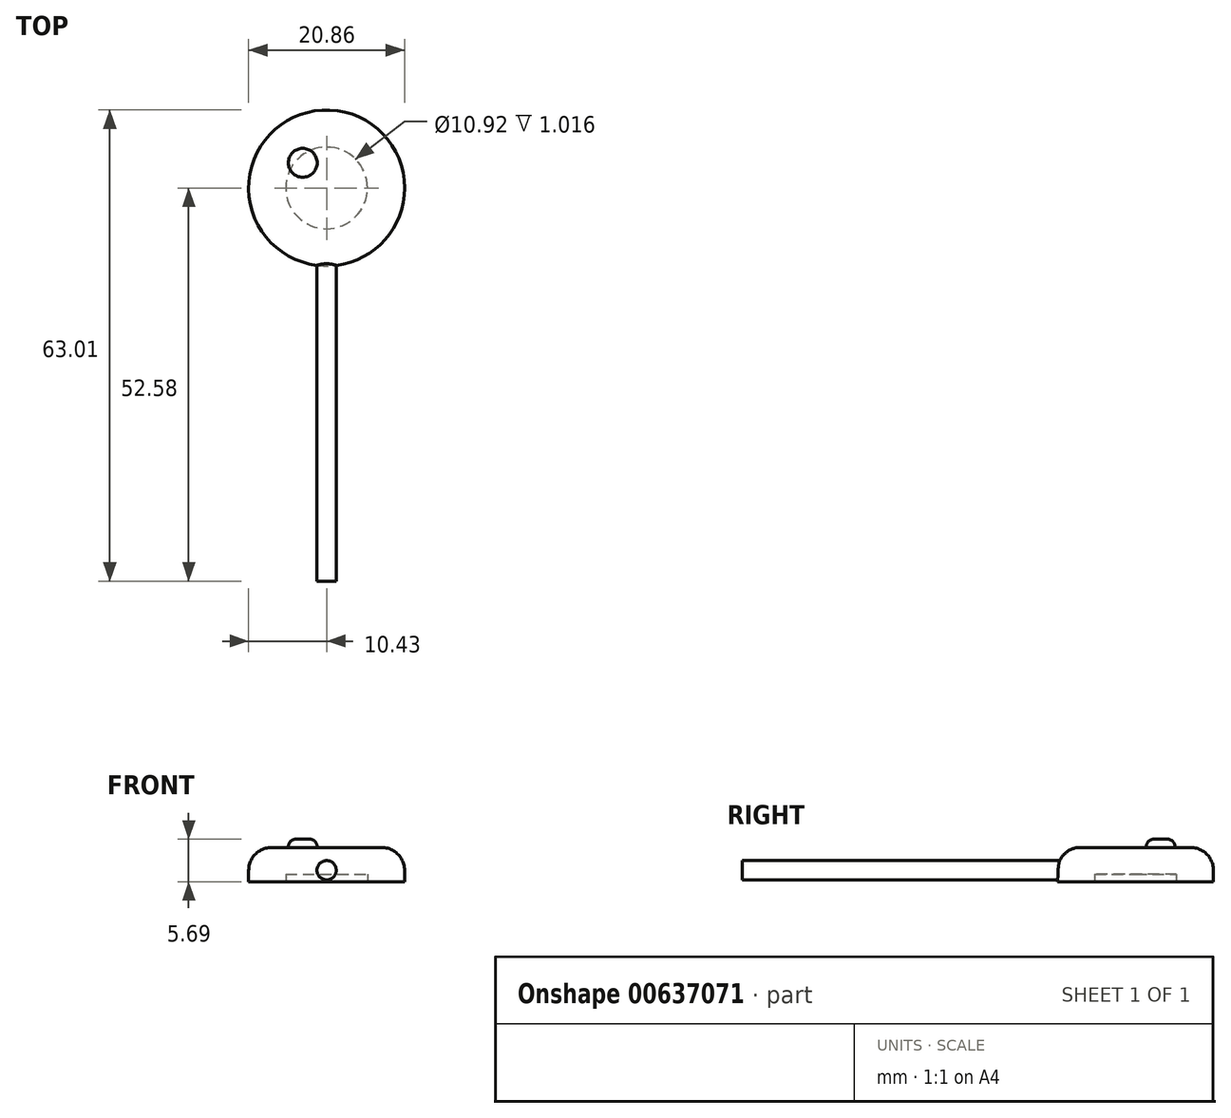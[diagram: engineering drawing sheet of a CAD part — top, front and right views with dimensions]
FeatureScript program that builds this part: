
annotation { "Feature Type Name" : "Feature", "Feature Type Description" : "" }
export const myFeature = defineFeature(function(context is Context, id is Id, definition is map)
    precondition{}
    {
        {
            var Q0;
            Q0=qCreatedBy(makeId("Top.planeOp"),FACE);
            var sketch = newSketch(context, id + "F0", { "sketchPlane" : qUnion([Q0])});
            skCircle(sketch, "E0", {"center": v(0, 0) * mm, "radius": 10.43 * mm});
            skSolve(sketch);
        }
        {
            var Q0;
            Q0=makeQuery(id+"F0.imprint","IMPRINT",FACE,{"disambiguationData":[TD([[makeQuery(id+"F0.imprint","IMPRINT",EDGE,{"derivedFrom":sQuery(id+"F0.wireOp",EDGE,"E0")}),1.0]])]});
            extrude(context, id + "F1", {"entities" : qUnion([Q0]), "depth" : 4.57 * mm, "offsetDistance" : 25.4 * mm});
        }
        {
            var Q0;
            Q0=makeQuery(id+"F1.opExtrude","CAP_EDGE",EDGE,{"disambiguationData":[OSD([sQuery(id+"F0.wireOp",EDGE,"E0")])],"isStart":false});
            fillet(context, id + "F2", {"entities" : qUnion([Q0]), "radius" : 3.07 * mm, "tangentPropagation" : true, "allowEdgeOverflow" : false});
        }
        {
            var Q0;
            Q0=qCreatedBy(makeId("Front.planeOp"),FACE);
            var sketch = newSketch(context, id + "F3", { "sketchPlane" : qUnion([Q0])});
            skCircle(sketch, "E1", {"center": v(0, 1.52) * mm, "radius": 1.29 * mm});
            skSolve(sketch);
        }
        {
            var Q0;
            Q0 = qSketchRegion(id + "F3", true);
            extrude(context, id + "F4", {"entities" : qUnion([Q0]), "operationType" : NewBodyOperationType.ADD, "depth" : 52.58 * mm, "offsetDistance" : 25.4 * mm});
        }
        {
            var Q0;
            Q0=makeQuery(id+"F1.opExtrude","CAP_FACE",FACE,{"disambiguationData":[OSD([sQuery(id+"F0.wireOp",EDGE,"E0")])],"isStart":false});
            var sketch = newSketch(context, id + "F5", { "sketchPlane" : qUnion([Q0])});
            skCircle(sketch, "E2", {"center": v(-3.2, 3.36) * mm, "radius": 1.93 * mm});
            skSolve(sketch);
        }
        {
            var Q0;
            Q0 = qSketchRegion(id + "F5", true);
            extrude(context, id + "F6", {"entities" : qUnion([Q0]), "operationType" : NewBodyOperationType.ADD, "depth" : 1.12 * mm, "offsetDistance" : 25.4 * mm});
        }
        {
            var Q0;
            Q0=makeQuery(id+"F6.opExtrude","CAP_EDGE",EDGE,{"disambiguationData":[OSD([sQuery(id+"F5.wireOp",EDGE,"E2")])],"isStart":false});
            fillet(context, id + "F7", {"entities" : qUnion([Q0]), "radius" : 1.04 * mm, "tangentPropagation" : true, "allowEdgeOverflow" : false});
        }
        {
            var Q0;
            Q0=makeQuery(id+"F1.opExtrude","CAP_FACE",FACE,{"disambiguationData":[OSD([sQuery(id+"F0.wireOp",EDGE,"E0")])],"isStart":true});
            var sketch = newSketch(context, id + "F8", { "sketchPlane" : qUnion([Q0])});
            skCircle(sketch, "E3", {"center": v(0, 0) * mm, "radius": 5.46 * mm});
            skSolve(sketch);
        }
        {
            var Q0;
            Q0=makeQuery(id+"F8.imprint","IMPRINT",FACE,{"disambiguationData":[TD([[makeQuery(id+"F8.imprint","IMPRINT",EDGE,{"derivedFrom":sQuery(id+"F8.wireOp",EDGE,"E3")}),1.0]])]});
            var Q1;
            Q1=sQuery(id+"F8.wireOp",EDGE,"E3");
            extrude(context, id + "F9", {"entities" : qUnion([Q0]), "operationType" : NewBodyOperationType.REMOVE, "surfaceEntities" : qUnion([Q1]), "oppositeDirection" : true, "depth" : 1.02 * mm, "offsetDistance" : 25.4 * mm});
        }
    });
